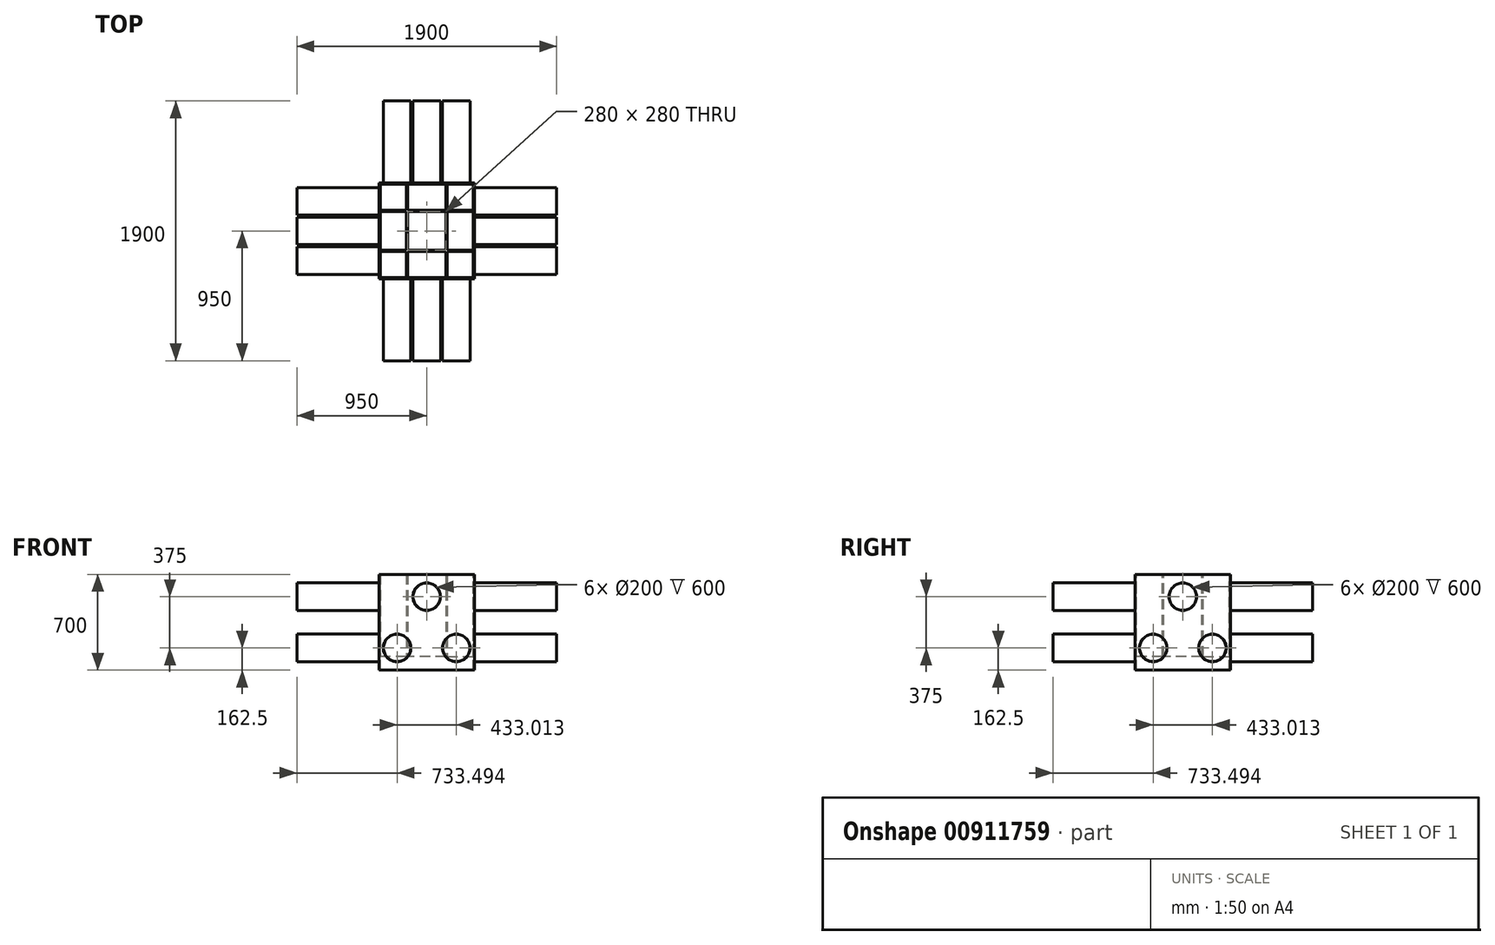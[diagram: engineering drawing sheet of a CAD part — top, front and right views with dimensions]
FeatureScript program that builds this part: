
annotation { "Feature Type Name" : "Feature", "Feature Type Description" : "" }
export const myFeature = defineFeature(function(context is Context, id is Id, definition is map)
    precondition{}
    {
        {
            var Q0;
            Q0=qCreatedBy(makeId("Top.planeOp"),FACE);
            var sketch = newSketch(context, id + "F0", { "sketchPlane" : qUnion([Q0])});
            skLineSegment(sketch, "E0.bottom", {"start": v(350, 350) * mm, "end": v(-350, 350) * mm});
            skLineSegment(sketch, "E0.top", {"start": v(350, -350) * mm, "end": v(-350, -350) * mm});
            skLineSegment(sketch, "E0.left", {"start": v(350, 350) * mm, "end": v(350, -350) * mm});
            skLineSegment(sketch, "E0.right", {"start": v(-350, 350) * mm, "end": v(-350, -350) * mm});
            skPoint(sketch, "E0.middle", {"position": v(0, 0) * mm});
            skLineSegment(sketch, "E1.bottom", {"start": v(340, 340) * mm, "end": v(-340, 340) * mm});
            skLineSegment(sketch, "E1.top", {"start": v(340, -340) * mm, "end": v(-340, -340) * mm});
            skLineSegment(sketch, "E1.left", {"start": v(340, 340) * mm, "end": v(340, -340) * mm});
            skLineSegment(sketch, "E1.right", {"start": v(-340, 340) * mm, "end": v(-340, -340) * mm});
            skSolve(sketch);
        }
        {
            var Q0;
            Q0=makeQuery(id+"F0.imprint","IMPRINT",FACE,{"disambiguationData":[TD([[makeQuery(id+"F0.imprint","IMPRINT",EDGE,{"derivedFrom":sQuery(id+"F0.wireOp",EDGE,"E0.bottom")}),1.0]])]});
            extrude(context, id + "F1", {"entities" : qUnion([Q0]), "oppositeDirection" : true, "depth" : 700 * mm, "offsetDistance" : 25 * mm});
        }
        {
            var Q0;
            Q0=qCreatedBy(makeId("Top.planeOp"),FACE);
            var sketch = newSketch(context, id + "F2", { "sketchPlane" : qUnion([Q0])});
            skLineSegment(sketch, "E2.bottom", {"start": v(-150, 150) * mm, "end": v(150, 150) * mm});
            skLineSegment(sketch, "E2.top", {"start": v(-150, -150) * mm, "end": v(150, -150) * mm});
            skLineSegment(sketch, "E2.left", {"start": v(-150, 150) * mm, "end": v(-150, -150) * mm});
            skLineSegment(sketch, "E2.right", {"start": v(150, 150) * mm, "end": v(150, -150) * mm});
            skPoint(sketch, "E2.middle", {"position": v(0, 0) * mm});
            skLineSegment(sketch, "E3", {"start": v(-150, 150) * mm, "end": v(-150, 300) * mm});
            skLineSegment(sketch, "E4", {"start": v(-150, -150) * mm, "end": v(-150, -300) * mm});
            skLineSegment(sketch, "E5", {"start": v(-150, -150) * mm, "end": v(-300, -150) * mm});
            skLineSegment(sketch, "E6", {"start": v(150, -150) * mm, "end": v(300, -150) * mm});
            skLineSegment(sketch, "E7", {"start": v(150, 150) * mm, "end": v(150, 300) * mm});
            skLineSegment(sketch, "E8", {"start": v(150, 150) * mm, "end": v(300, 150) * mm});
            skLineSegment(sketch, "E9", {"start": v(150, -150) * mm, "end": v(150, -300) * mm});
            skLineSegment(sketch, "E10", {"start": v(-150, 150) * mm, "end": v(-300, 150) * mm});
            skLineSegment(sketch, "E11.bottom", {"start": v(140, 140) * mm, "end": v(-140, 140) * mm});
            skLineSegment(sketch, "E11.top", {"start": v(140, -140) * mm, "end": v(-140, -140) * mm});
            skLineSegment(sketch, "E11.left", {"start": v(140, 140) * mm, "end": v(140, -140) * mm});
            skLineSegment(sketch, "E11.right", {"start": v(-140, 140) * mm, "end": v(-140, -140) * mm});
            skLineSegment(sketch, "E12", {"start": v(-140, 140) * mm, "end": v(-140, 300) * mm});
            skLineSegment(sketch, "E13", {"start": v(140, 140) * mm, "end": v(140, 300) * mm});
            skLineSegment(sketch, "E14", {"start": v(140, 140) * mm, "end": v(300, 140) * mm});
            skLineSegment(sketch, "E15", {"start": v(140, -140) * mm, "end": v(300, -140) * mm});
            skLineSegment(sketch, "E16", {"start": v(140, -140) * mm, "end": v(140, -300) * mm});
            skLineSegment(sketch, "E17", {"start": v(-140, -140) * mm, "end": v(-140, -300) * mm});
            skLineSegment(sketch, "E18", {"start": v(-140, 140) * mm, "end": v(-300, 140) * mm});
            skLineSegment(sketch, "E19", {"start": v(-140, -140) * mm, "end": v(-300, -140) * mm});
            skLineSegment(sketch, "E20", {"start": v(-300, 150) * mm, "end": v(-300, 140) * mm});
            skLineSegment(sketch, "E21", {"start": v(-300, -140) * mm, "end": v(-300, -150) * mm});
            skLineSegment(sketch, "E22", {"start": v(-150, -300) * mm, "end": v(-140, -300) * mm});
            skLineSegment(sketch, "E23", {"start": v(140, -300) * mm, "end": v(150, -300) * mm});
            skLineSegment(sketch, "E24", {"start": v(300, -150) * mm, "end": v(300, -140) * mm});
            skLineSegment(sketch, "E25", {"start": v(300, 140) * mm, "end": v(300, 150) * mm});
            skLineSegment(sketch, "E26", {"start": v(140, 300) * mm, "end": v(150, 300) * mm});
            skLineSegment(sketch, "E27", {"start": v(-150, 300) * mm, "end": v(-140, 300) * mm});
            skSolve(sketch);
        }
        {
            var Q0;
            {var subQ0=sQuery(id+"F2.wireOp",EDGE,"E3");Q0=makeQuery(id+"F2.imprint","IMPRINT",FACE,{"disambiguationData":[TD([[makeQuery(id+"F2.imprint","IMPRINT",EDGE,{"derivedFrom":subQ0}),-1.0]])]});}
            var Q1;
            {var subQ0=sQuery(id+"F2.wireOp",EDGE,"E10");Q1=makeQuery(id+"F2.imprint","IMPRINT",FACE,{"disambiguationData":[TD([[makeQuery(id+"F2.imprint","IMPRINT",EDGE,{"derivedFrom":subQ0}),1.0]])]});}
            var Q2;
            {var subQ1=sQuery(id+"F2.wireOp",EDGE,"E2.bottom");var subQ3=sQuery(id+"F2.wireOp",EDGE,"E12");var subQ4=makeQuery(id+"F2.imprint","INTERSECT",VERTEX,{"derivedFrom":[subQ1,subQ3]});Q2=makeQuery(id+"F2.imprint","IMPRINT",FACE,{"disambiguationData":[TD([[makeQuery(id+"F2.imprint","IMPRINT",EDGE,{"disambiguationData":[TD([[subQ4,1.0]])],"derivedFrom":subQ1}),-1.0]])]});}
            var Q3;
            {var subQ5=sQuery(id+"F2.wireOp",EDGE,"E11.bottom");Q3=makeQuery(id+"F2.imprint","IMPRINT",FACE,{"disambiguationData":[TD([[makeQuery(id+"F2.imprint","IMPRINT",EDGE,{"derivedFrom":subQ5}),-1.0]])]});}
            var Q4;
            {var subQ5=sQuery(id+"F2.wireOp",EDGE,"E11.right");Q4=makeQuery(id+"F2.imprint","IMPRINT",FACE,{"disambiguationData":[TD([[makeQuery(id+"F2.imprint","IMPRINT",EDGE,{"derivedFrom":subQ5}),-1.0]])]});}
            var Q5;
            {var subQ0=sQuery(id+"F2.wireOp",EDGE,"E7");Q5=makeQuery(id+"F2.imprint","IMPRINT",FACE,{"disambiguationData":[TD([[makeQuery(id+"F2.imprint","IMPRINT",EDGE,{"derivedFrom":subQ0}),1.0]])]});}
            var Q6;
            {var subQ0=sQuery(id+"F2.wireOp",EDGE,"E8");Q6=makeQuery(id+"F2.imprint","IMPRINT",FACE,{"disambiguationData":[TD([[makeQuery(id+"F2.imprint","IMPRINT",EDGE,{"derivedFrom":subQ0}),-1.0]])]});}
            var Q7;
            {var subQ1=sQuery(id+"F2.wireOp",EDGE,"E2.bottom");var subQ3=sQuery(id+"F2.wireOp",EDGE,"E13");var subQ4=makeQuery(id+"F2.imprint","INTERSECT",VERTEX,{"derivedFrom":[subQ1,subQ3]});Q7=makeQuery(id+"F2.imprint","IMPRINT",FACE,{"disambiguationData":[TD([[makeQuery(id+"F2.imprint","IMPRINT",EDGE,{"disambiguationData":[TD([[subQ4,-1.0]])],"derivedFrom":subQ1}),-1.0]])]});}
            var Q8;
            {var subQ0=sQuery(id+"F2.wireOp",EDGE,"E9");Q8=makeQuery(id+"F2.imprint","IMPRINT",FACE,{"disambiguationData":[TD([[makeQuery(id+"F2.imprint","IMPRINT",EDGE,{"derivedFrom":subQ0}),-1.0]])]});}
            var Q9;
            {var subQ0=sQuery(id+"F2.wireOp",EDGE,"E6");Q9=makeQuery(id+"F2.imprint","IMPRINT",FACE,{"disambiguationData":[TD([[makeQuery(id+"F2.imprint","IMPRINT",EDGE,{"derivedFrom":subQ0}),1.0]])]});}
            var Q10;
            {var subQ1=sQuery(id+"F2.wireOp",EDGE,"E2.top");var subQ3=sQuery(id+"F2.wireOp",EDGE,"E16");var subQ4=makeQuery(id+"F2.imprint","INTERSECT",VERTEX,{"derivedFrom":[subQ1,subQ3]});Q10=makeQuery(id+"F2.imprint","IMPRINT",FACE,{"disambiguationData":[TD([[makeQuery(id+"F2.imprint","IMPRINT",EDGE,{"disambiguationData":[TD([[subQ4,-1.0]])],"derivedFrom":subQ1}),1.0]])]});}
            var Q11;
            {var subQ5=sQuery(id+"F2.wireOp",EDGE,"E11.left");Q11=makeQuery(id+"F2.imprint","IMPRINT",FACE,{"disambiguationData":[TD([[makeQuery(id+"F2.imprint","IMPRINT",EDGE,{"derivedFrom":subQ5}),1.0]])]});}
            var Q12;
            {var subQ5=sQuery(id+"F2.wireOp",EDGE,"E11.top");Q12=makeQuery(id+"F2.imprint","IMPRINT",FACE,{"disambiguationData":[TD([[makeQuery(id+"F2.imprint","IMPRINT",EDGE,{"derivedFrom":subQ5}),1.0]])]});}
            var Q13;
            {var subQ0=sQuery(id+"F2.wireOp",EDGE,"E5");Q13=makeQuery(id+"F2.imprint","IMPRINT",FACE,{"disambiguationData":[TD([[makeQuery(id+"F2.imprint","IMPRINT",EDGE,{"derivedFrom":subQ0}),-1.0]])]});}
            var Q14;
            {var subQ0=sQuery(id+"F2.wireOp",EDGE,"E4");Q14=makeQuery(id+"F2.imprint","IMPRINT",FACE,{"disambiguationData":[TD([[makeQuery(id+"F2.imprint","IMPRINT",EDGE,{"derivedFrom":subQ0}),1.0]])]});}
            var Q15;
            {var subQ1=sQuery(id+"F2.wireOp",EDGE,"E2.top");var subQ3=sQuery(id+"F2.wireOp",EDGE,"E17");var subQ4=makeQuery(id+"F2.imprint","INTERSECT",VERTEX,{"derivedFrom":[subQ1,subQ3]});Q15=makeQuery(id+"F2.imprint","IMPRINT",FACE,{"disambiguationData":[TD([[makeQuery(id+"F2.imprint","IMPRINT",EDGE,{"disambiguationData":[TD([[subQ4,1.0]])],"derivedFrom":subQ1}),1.0]])]});}
            extrude(context, id + "F3", {"entities" : qUnion([Q0, Q1, Q2, Q3, Q4, Q5, Q6, Q7, Q8, Q9, Q10, Q11, Q12, Q13, Q14, Q15]), "operationType" : NewBodyOperationType.ADD, "oppositeDirection" : true, "depth" : 600 * mm, "offsetDistance" : 25 * mm});
        }
        {
            var Q0;
            Q0=makeQuery(id+"F1.opExtrude","SWEPT_FACE",FACE,{"disambiguationData":[OSD([sQuery(id+"F0.wireOp",EDGE,"E0.left")])]});
            var sketch = newSketch(context, id + "F4", { "sketchPlane" : qUnion([Q0])});
            skPoint(sketch, "E28", {"position": v(0, -350) * mm});
            skPoint(sketch, "E28.positionSnap0", {"position": v(-350, -350) * mm});
            skPoint(sketch, "E28.positionSnap1", {"position": v(0, 0) * mm});
            skCircle(sketch, "E29.cCircle", {"center": v(0, -412.5) * mm, "radius": 250 * mm, "construction": true});
            skLineSegment(sketch, "E29.0", {"start": v(0, -162.5) * mm, "end": v(216.5, -537.5) * mm});
            skLineSegment(sketch, "E29.1", {"start": v(216.5, -537.5) * mm, "end": v(-216.5, -537.5) * mm});
            skLineSegment(sketch, "E29.2", {"start": v(-216.5, -537.5) * mm, "end": v(0, -162.5) * mm});
            skCircle(sketch, "E30", {"center": v(0, -162.5) * mm, "radius": 100 * mm});
            skCircle(sketch, "E31", {"center": v(216.5, -537.5) * mm, "radius": 100 * mm});
            skCircle(sketch, "E32", {"center": v(-216.5, -537.5) * mm, "radius": 100 * mm});
            skCircle(sketch, "E33", {"center": v(0, -162.5) * mm, "radius": 101 * mm});
            skCircle(sketch, "E34", {"center": v(-216.5, -537.5) * mm, "radius": 101 * mm});
            skCircle(sketch, "E35", {"center": v(216.5, -537.5) * mm, "radius": 101 * mm});
            skSolve(sketch);
        }
        {
            var Q0;
            Q0=makeQuery(id+"F1.opExtrude","SWEPT_FACE",FACE,{"disambiguationData":[OSD([sQuery(id+"F0.wireOp",EDGE,"E0.top")])]});
            var sketch = newSketch(context, id + "F5", { "sketchPlane" : qUnion([Q0])});
            skPoint(sketch, "E36", {"position": v(0, -412.5) * mm});
            skPoint(sketch, "E36.positionSnap0", {"position": v(-350, -412.5) * mm});
            skPoint(sketch, "E36.positionSnap1", {"position": v(0, 157.53) * mm});
            skCircle(sketch, "E37.cCircle", {"center": v(0, -412.5) * mm, "radius": 250 * mm, "construction": true});
            skLineSegment(sketch, "E37.0", {"start": v(0, -162.5) * mm, "end": v(216.5, -537.5) * mm});
            skLineSegment(sketch, "E37.1", {"start": v(216.5, -537.5) * mm, "end": v(-216.5, -537.5) * mm});
            skLineSegment(sketch, "E37.2", {"start": v(-216.5, -537.5) * mm, "end": v(0, -162.5) * mm});
            skCircle(sketch, "E38", {"center": v(0, -162.5) * mm, "radius": 100 * mm});
            skCircle(sketch, "E39", {"center": v(216.5, -537.5) * mm, "radius": 100 * mm});
            skCircle(sketch, "E40", {"center": v(-216.5, -537.5) * mm, "radius": 100 * mm});
            skCircle(sketch, "E41", {"center": v(0, -162.5) * mm, "radius": 101 * mm});
            skCircle(sketch, "E42", {"center": v(-216.5, -537.5) * mm, "radius": 101 * mm});
            skCircle(sketch, "E43", {"center": v(216.5, -537.5) * mm, "radius": 101 * mm});
            skSolve(sketch);
        }
        {
            var Q0;
            Q0=makeQuery(id+"F1.opExtrude","SWEPT_FACE",FACE,{"disambiguationData":[OSD([sQuery(id+"F0.wireOp",EDGE,"E0.right")])]});
            var sketch = newSketch(context, id + "F6", { "sketchPlane" : qUnion([Q0])});
            skPoint(sketch, "E44", {"position": v(0, -350) * mm});
            skPoint(sketch, "E44.positionSnap0", {"position": v(-350, -350) * mm});
            skPoint(sketch, "E44.positionSnap1", {"position": v(0, 0) * mm});
            skCircle(sketch, "E45.cCircle", {"center": v(0, -412.5) * mm, "radius": 250 * mm, "construction": true});
            skLineSegment(sketch, "E45.0", {"start": v(0, -162.5) * mm, "end": v(216.5, -537.5) * mm});
            skLineSegment(sketch, "E45.1", {"start": v(216.5, -537.5) * mm, "end": v(-216.5, -537.5) * mm});
            skLineSegment(sketch, "E45.2", {"start": v(-216.5, -537.5) * mm, "end": v(0, -162.5) * mm});
            skCircle(sketch, "E46", {"center": v(0, -162.5) * mm, "radius": 100 * mm});
            skCircle(sketch, "E47", {"center": v(216.5, -537.5) * mm, "radius": 100 * mm});
            skCircle(sketch, "E48", {"center": v(-216.5, -537.5) * mm, "radius": 100 * mm});
            skCircle(sketch, "E49", {"center": v(0, -162.5) * mm, "radius": 101 * mm});
            skCircle(sketch, "E50", {"center": v(-216.5, -537.5) * mm, "radius": 101 * mm});
            skCircle(sketch, "E51", {"center": v(216.5, -537.5) * mm, "radius": 101 * mm});
            skSolve(sketch);
        }
        {
            var Q0;
            Q0=makeQuery(id+"F1.opExtrude","SWEPT_FACE",FACE,{"disambiguationData":[OSD([sQuery(id+"F0.wireOp",EDGE,"E0.bottom")])]});
            var sketch = newSketch(context, id + "F7", { "sketchPlane" : qUnion([Q0])});
            skPoint(sketch, "E52", {"position": v(0, -350) * mm});
            skPoint(sketch, "E52.positionSnap0", {"position": v(-350, -350) * mm});
            skPoint(sketch, "E52.positionSnap1", {"position": v(0, 0) * mm});
            skCircle(sketch, "E53.cCircle", {"center": v(0, -412.5) * mm, "radius": 250 * mm, "construction": true});
            skLineSegment(sketch, "E53.0", {"start": v(0, -162.5) * mm, "end": v(216.5, -537.5) * mm});
            skLineSegment(sketch, "E53.1", {"start": v(216.5, -537.5) * mm, "end": v(-216.5, -537.5) * mm});
            skLineSegment(sketch, "E53.2", {"start": v(-216.5, -537.5) * mm, "end": v(0, -162.5) * mm});
            skCircle(sketch, "E54", {"center": v(0, -162.5) * mm, "radius": 100 * mm});
            skCircle(sketch, "E55", {"center": v(216.5, -537.5) * mm, "radius": 100 * mm});
            skCircle(sketch, "E56", {"center": v(-216.5, -537.5) * mm, "radius": 100 * mm});
            skCircle(sketch, "E57", {"center": v(0, -162.5) * mm, "radius": 101 * mm});
            skCircle(sketch, "E58", {"center": v(216.5, -537.5) * mm, "radius": 101 * mm});
            skCircle(sketch, "E59", {"center": v(-216.5, -537.5) * mm, "radius": 101 * mm});
            skSolve(sketch);
        }
        {
            var Q0;
            Q0=makeQuery(id+"F3.opExtrude","SWEPT_FACE",FACE,{"disambiguationData":[OSD([sQuery(id+"F2.wireOp",EDGE,"E20")])]});
            extrude(context, id + "F8", {"entities" : qUnion([Q0]), "depth" : 50 * mm, "offsetDistance" : 25 * mm});
        }
        {
            var Q0;
            Q0=makeQuery(id+"F3.opExtrude","SWEPT_FACE",FACE,{"disambiguationData":[OSD([sQuery(id+"F2.wireOp",EDGE,"E22")])]});
            extrude(context, id + "F9", {"entities" : qUnion([Q0]), "depth" : 50 * mm, "offsetDistance" : 25 * mm});
        }
        {
            var Q0;
            Q0=makeQuery(id+"F3.opExtrude","SWEPT_FACE",FACE,{"disambiguationData":[OSD([sQuery(id+"F2.wireOp",EDGE,"E21")])]});
            extrude(context, id + "F10", {"entities" : qUnion([Q0]), "operationType" : NewBodyOperationType.ADD, "depth" : 50 * mm, "offsetDistance" : 25 * mm});
        }
        {
            var Q0;
            Q0=makeQuery(id+"F3.opExtrude","SWEPT_FACE",FACE,{"disambiguationData":[OSD([sQuery(id+"F2.wireOp",EDGE,"E23")])]});
            extrude(context, id + "F11", {"entities" : qUnion([Q0]), "depth" : 50 * mm, "offsetDistance" : 25 * mm});
        }
        {
            var Q0;
            Q0=makeQuery(id+"F3.opExtrude","SWEPT_FACE",FACE,{"disambiguationData":[OSD([sQuery(id+"F2.wireOp",EDGE,"E24")])]});
            extrude(context, id + "F12", {"entities" : qUnion([Q0]), "depth" : 50 * mm, "offsetDistance" : 25 * mm});
        }
        {
            var Q0;
            Q0=makeQuery(id+"F3.opExtrude","SWEPT_FACE",FACE,{"disambiguationData":[OSD([sQuery(id+"F2.wireOp",EDGE,"E25")])]});
            extrude(context, id + "F13", {"entities" : qUnion([Q0]), "depth" : 50 * mm, "offsetDistance" : 25 * mm});
        }
        {
            var Q0;
            Q0=makeQuery(id+"F3.opExtrude","SWEPT_FACE",FACE,{"disambiguationData":[OSD([sQuery(id+"F2.wireOp",EDGE,"E26")])]});
            extrude(context, id + "F14", {"entities" : qUnion([Q0]), "depth" : 50 * mm, "offsetDistance" : 25 * mm});
        }
        {
            var Q0;
            Q0=makeQuery(id+"F3.opExtrude","SWEPT_FACE",FACE,{"disambiguationData":[OSD([sQuery(id+"F2.wireOp",EDGE,"E27")])]});
            extrude(context, id + "F15", {"entities" : qUnion([Q0]), "depth" : 50 * mm, "offsetDistance" : 25 * mm});
        }
        {
            var Q0;
            {var subQ0=sQuery(id+"F4.wireOp",EDGE,"E30");var subQ1=sQuery(id+"F4.wireOp",EDGE,"E29.0");var subQ2=makeQuery(id+"F4.imprint","INTERSECT",VERTEX,{"derivedFrom":[subQ1,subQ0]});Q0=makeQuery(id+"F4.imprint","IMPRINT",FACE,{"disambiguationData":[TD([[makeQuery(id+"F4.imprint","IMPRINT",EDGE,{"disambiguationData":[TD([[subQ2,-1.0]])],"derivedFrom":subQ1}),1.0]])]});}
            var Q1;
            {var subQ0=sQuery(id+"F4.wireOp",EDGE,"E35");var subQ1=sQuery(id+"F4.wireOp",EDGE,"E29.0");var subQ2=makeQuery(id+"F4.imprint","INTERSECT",VERTEX,{"derivedFrom":[subQ1,subQ0]});Q1=makeQuery(id+"F4.imprint","IMPRINT",FACE,{"disambiguationData":[TD([[makeQuery(id+"F4.imprint","IMPRINT",EDGE,{"disambiguationData":[TD([[subQ2,-1.0]])],"derivedFrom":subQ1}),1.0]])]});}
            var Q2;
            {var subQ0=sQuery(id+"F4.wireOp",EDGE,"E35");var subQ1=sQuery(id+"F4.wireOp",EDGE,"E29.0");var subQ2=makeQuery(id+"F4.imprint","INTERSECT",VERTEX,{"derivedFrom":[subQ1,subQ0]});Q2=makeQuery(id+"F4.imprint","IMPRINT",FACE,{"disambiguationData":[TD([[makeQuery(id+"F4.imprint","IMPRINT",EDGE,{"disambiguationData":[TD([[subQ2,-1.0]])],"derivedFrom":subQ1}),-1.0]])]});}
            var Q3;
            {var subQ0=sQuery(id+"F4.wireOp",EDGE,"E30");var subQ1=sQuery(id+"F4.wireOp",EDGE,"E29.0");var subQ2=makeQuery(id+"F4.imprint","INTERSECT",VERTEX,{"derivedFrom":[subQ1,subQ0]});Q3=makeQuery(id+"F4.imprint","IMPRINT",FACE,{"disambiguationData":[TD([[makeQuery(id+"F4.imprint","IMPRINT",EDGE,{"disambiguationData":[TD([[subQ2,-1.0]])],"derivedFrom":subQ1}),-1.0]])]});}
            var Q4;
            {var subQ0=sQuery(id+"F4.wireOp",EDGE,"E34");var subQ1=sQuery(id+"F4.wireOp",EDGE,"E29.1");var subQ2=makeQuery(id+"F4.imprint","INTERSECT",VERTEX,{"derivedFrom":[subQ1,subQ0]});Q4=makeQuery(id+"F4.imprint","IMPRINT",FACE,{"disambiguationData":[TD([[makeQuery(id+"F4.imprint","IMPRINT",EDGE,{"disambiguationData":[TD([[subQ2,-1.0]])],"derivedFrom":subQ1}),1.0]])]});}
            var Q5;
            {var subQ0=sQuery(id+"F4.wireOp",EDGE,"E34");var subQ1=sQuery(id+"F4.wireOp",EDGE,"E29.1");var subQ2=makeQuery(id+"F4.imprint","INTERSECT",VERTEX,{"derivedFrom":[subQ1,subQ0]});Q5=makeQuery(id+"F4.imprint","IMPRINT",FACE,{"disambiguationData":[TD([[makeQuery(id+"F4.imprint","IMPRINT",EDGE,{"disambiguationData":[TD([[subQ2,-1.0]])],"derivedFrom":subQ1}),-1.0]])]});}
            extrude(context, id + "F16", {"entities" : qUnion([Q0, Q1, Q2, Q3, Q4, Q5]), "operationType" : NewBodyOperationType.ADD, "depth" : 600 * mm, "offsetDistance" : 25 * mm});
        }
        {
            var Q0;
            {var subQ0=sQuery(id+"F5.wireOp",EDGE,"E38");var subQ1=sQuery(id+"F5.wireOp",EDGE,"E37.0");var subQ2=makeQuery(id+"F5.imprint","INTERSECT",VERTEX,{"derivedFrom":[subQ1,subQ0]});Q0=makeQuery(id+"F5.imprint","IMPRINT",FACE,{"disambiguationData":[TD([[makeQuery(id+"F5.imprint","IMPRINT",EDGE,{"disambiguationData":[TD([[subQ2,-1.0]])],"derivedFrom":subQ1}),-1.0]])]});}
            var Q1;
            {var subQ0=sQuery(id+"F5.wireOp",EDGE,"E38");var subQ1=sQuery(id+"F5.wireOp",EDGE,"E37.0");var subQ2=makeQuery(id+"F5.imprint","INTERSECT",VERTEX,{"derivedFrom":[subQ1,subQ0]});Q1=makeQuery(id+"F5.imprint","IMPRINT",FACE,{"disambiguationData":[TD([[makeQuery(id+"F5.imprint","IMPRINT",EDGE,{"disambiguationData":[TD([[subQ2,-1.0]])],"derivedFrom":subQ1}),1.0]])]});}
            var Q2;
            {var subQ0=sQuery(id+"F5.wireOp",EDGE,"E42");var subQ1=sQuery(id+"F5.wireOp",EDGE,"E37.1");var subQ2=makeQuery(id+"F5.imprint","INTERSECT",VERTEX,{"derivedFrom":[subQ1,subQ0]});Q2=makeQuery(id+"F5.imprint","IMPRINT",FACE,{"disambiguationData":[TD([[makeQuery(id+"F5.imprint","IMPRINT",EDGE,{"disambiguationData":[TD([[subQ2,-1.0]])],"derivedFrom":subQ1}),1.0]])]});}
            var Q3;
            {var subQ0=sQuery(id+"F5.wireOp",EDGE,"E42");var subQ1=sQuery(id+"F5.wireOp",EDGE,"E37.1");var subQ2=makeQuery(id+"F5.imprint","INTERSECT",VERTEX,{"derivedFrom":[subQ1,subQ0]});Q3=makeQuery(id+"F5.imprint","IMPRINT",FACE,{"disambiguationData":[TD([[makeQuery(id+"F5.imprint","IMPRINT",EDGE,{"disambiguationData":[TD([[subQ2,-1.0]])],"derivedFrom":subQ1}),-1.0]])]});}
            var Q4;
            {var subQ0=sQuery(id+"F5.wireOp",EDGE,"E43");var subQ1=sQuery(id+"F5.wireOp",EDGE,"E37.0");var subQ2=makeQuery(id+"F5.imprint","INTERSECT",VERTEX,{"derivedFrom":[subQ1,subQ0]});Q4=makeQuery(id+"F5.imprint","IMPRINT",FACE,{"disambiguationData":[TD([[makeQuery(id+"F5.imprint","IMPRINT",EDGE,{"disambiguationData":[TD([[subQ2,-1.0]])],"derivedFrom":subQ1}),1.0]])]});}
            var Q5;
            {var subQ0=sQuery(id+"F5.wireOp",EDGE,"E43");var subQ1=sQuery(id+"F5.wireOp",EDGE,"E37.0");var subQ2=makeQuery(id+"F5.imprint","INTERSECT",VERTEX,{"derivedFrom":[subQ1,subQ0]});Q5=makeQuery(id+"F5.imprint","IMPRINT",FACE,{"disambiguationData":[TD([[makeQuery(id+"F5.imprint","IMPRINT",EDGE,{"disambiguationData":[TD([[subQ2,-1.0]])],"derivedFrom":subQ1}),-1.0]])]});}
            extrude(context, id + "F17", {"entities" : qUnion([Q0, Q1, Q2, Q3, Q4, Q5]), "operationType" : NewBodyOperationType.ADD, "depth" : 600 * mm, "offsetDistance" : 25 * mm});
        }
        {
            var Q0;
            {var subQ0=sQuery(id+"F6.wireOp",EDGE,"E46");var subQ1=sQuery(id+"F6.wireOp",EDGE,"E45.0");var subQ2=makeQuery(id+"F6.imprint","INTERSECT",VERTEX,{"derivedFrom":[subQ1,subQ0]});Q0=makeQuery(id+"F6.imprint","IMPRINT",FACE,{"disambiguationData":[TD([[makeQuery(id+"F6.imprint","IMPRINT",EDGE,{"disambiguationData":[TD([[subQ2,-1.0]])],"derivedFrom":subQ1}),1.0]])]});}
            var Q1;
            {var subQ0=sQuery(id+"F6.wireOp",EDGE,"E46");var subQ1=sQuery(id+"F6.wireOp",EDGE,"E45.0");var subQ2=makeQuery(id+"F6.imprint","INTERSECT",VERTEX,{"derivedFrom":[subQ1,subQ0]});Q1=makeQuery(id+"F6.imprint","IMPRINT",FACE,{"disambiguationData":[TD([[makeQuery(id+"F6.imprint","IMPRINT",EDGE,{"disambiguationData":[TD([[subQ2,-1.0]])],"derivedFrom":subQ1}),-1.0]])]});}
            var Q2;
            {var subQ0=sQuery(id+"F6.wireOp",EDGE,"E51");var subQ1=sQuery(id+"F6.wireOp",EDGE,"E45.0");var subQ2=makeQuery(id+"F6.imprint","INTERSECT",VERTEX,{"derivedFrom":[subQ1,subQ0]});Q2=makeQuery(id+"F6.imprint","IMPRINT",FACE,{"disambiguationData":[TD([[makeQuery(id+"F6.imprint","IMPRINT",EDGE,{"disambiguationData":[TD([[subQ2,-1.0]])],"derivedFrom":subQ1}),1.0]])]});}
            var Q3;
            {var subQ0=sQuery(id+"F6.wireOp",EDGE,"E51");var subQ1=sQuery(id+"F6.wireOp",EDGE,"E45.0");var subQ2=makeQuery(id+"F6.imprint","INTERSECT",VERTEX,{"derivedFrom":[subQ1,subQ0]});Q3=makeQuery(id+"F6.imprint","IMPRINT",FACE,{"disambiguationData":[TD([[makeQuery(id+"F6.imprint","IMPRINT",EDGE,{"disambiguationData":[TD([[subQ2,-1.0]])],"derivedFrom":subQ1}),-1.0]])]});}
            var Q4;
            {var subQ0=sQuery(id+"F6.wireOp",EDGE,"E50");var subQ1=sQuery(id+"F6.wireOp",EDGE,"E45.1");var subQ2=makeQuery(id+"F6.imprint","INTERSECT",VERTEX,{"derivedFrom":[subQ1,subQ0]});Q4=makeQuery(id+"F6.imprint","IMPRINT",FACE,{"disambiguationData":[TD([[makeQuery(id+"F6.imprint","IMPRINT",EDGE,{"disambiguationData":[TD([[subQ2,-1.0]])],"derivedFrom":subQ1}),1.0]])]});}
            var Q5;
            {var subQ0=sQuery(id+"F6.wireOp",EDGE,"E50");var subQ1=sQuery(id+"F6.wireOp",EDGE,"E45.1");var subQ2=makeQuery(id+"F6.imprint","INTERSECT",VERTEX,{"derivedFrom":[subQ1,subQ0]});Q5=makeQuery(id+"F6.imprint","IMPRINT",FACE,{"disambiguationData":[TD([[makeQuery(id+"F6.imprint","IMPRINT",EDGE,{"disambiguationData":[TD([[subQ2,-1.0]])],"derivedFrom":subQ1}),-1.0]])]});}
            extrude(context, id + "F18", {"entities" : qUnion([Q0, Q1, Q2, Q3, Q4, Q5]), "operationType" : NewBodyOperationType.ADD, "depth" : 600 * mm, "offsetDistance" : 25 * mm});
        }
        {
            var Q0;
            {var subQ0=sQuery(id+"F7.wireOp",EDGE,"E54");var subQ1=sQuery(id+"F7.wireOp",EDGE,"E53.0");var subQ2=makeQuery(id+"F7.imprint","INTERSECT",VERTEX,{"derivedFrom":[subQ1,subQ0]});Q0=makeQuery(id+"F7.imprint","IMPRINT",FACE,{"disambiguationData":[TD([[makeQuery(id+"F7.imprint","IMPRINT",EDGE,{"disambiguationData":[TD([[subQ2,-1.0]])],"derivedFrom":subQ1}),-1.0]])]});}
            var Q1;
            {var subQ0=sQuery(id+"F7.wireOp",EDGE,"E54");var subQ1=sQuery(id+"F7.wireOp",EDGE,"E53.0");var subQ2=makeQuery(id+"F7.imprint","INTERSECT",VERTEX,{"derivedFrom":[subQ1,subQ0]});Q1=makeQuery(id+"F7.imprint","IMPRINT",FACE,{"disambiguationData":[TD([[makeQuery(id+"F7.imprint","IMPRINT",EDGE,{"disambiguationData":[TD([[subQ2,-1.0]])],"derivedFrom":subQ1}),1.0]])]});}
            var Q2;
            {var subQ0=sQuery(id+"F7.wireOp",EDGE,"E59");var subQ1=sQuery(id+"F7.wireOp",EDGE,"E53.1");var subQ2=makeQuery(id+"F7.imprint","INTERSECT",VERTEX,{"derivedFrom":[subQ1,subQ0]});Q2=makeQuery(id+"F7.imprint","IMPRINT",FACE,{"disambiguationData":[TD([[makeQuery(id+"F7.imprint","IMPRINT",EDGE,{"disambiguationData":[TD([[subQ2,-1.0]])],"derivedFrom":subQ1}),1.0]])]});}
            var Q3;
            {var subQ0=sQuery(id+"F7.wireOp",EDGE,"E59");var subQ1=sQuery(id+"F7.wireOp",EDGE,"E53.1");var subQ2=makeQuery(id+"F7.imprint","INTERSECT",VERTEX,{"derivedFrom":[subQ1,subQ0]});Q3=makeQuery(id+"F7.imprint","IMPRINT",FACE,{"disambiguationData":[TD([[makeQuery(id+"F7.imprint","IMPRINT",EDGE,{"disambiguationData":[TD([[subQ2,-1.0]])],"derivedFrom":subQ1}),-1.0]])]});}
            var Q4;
            {var subQ0=sQuery(id+"F7.wireOp",EDGE,"E58");var subQ1=sQuery(id+"F7.wireOp",EDGE,"E53.0");var subQ2=makeQuery(id+"F7.imprint","INTERSECT",VERTEX,{"derivedFrom":[subQ1,subQ0]});Q4=makeQuery(id+"F7.imprint","IMPRINT",FACE,{"disambiguationData":[TD([[makeQuery(id+"F7.imprint","IMPRINT",EDGE,{"disambiguationData":[TD([[subQ2,-1.0]])],"derivedFrom":subQ1}),-1.0]])]});}
            var Q5;
            {var subQ0=sQuery(id+"F7.wireOp",EDGE,"E58");var subQ1=sQuery(id+"F7.wireOp",EDGE,"E53.0");var subQ2=makeQuery(id+"F7.imprint","INTERSECT",VERTEX,{"derivedFrom":[subQ1,subQ0]});Q5=makeQuery(id+"F7.imprint","IMPRINT",FACE,{"disambiguationData":[TD([[makeQuery(id+"F7.imprint","IMPRINT",EDGE,{"disambiguationData":[TD([[subQ2,-1.0]])],"derivedFrom":subQ1}),1.0]])]});}
            extrude(context, id + "F19", {"entities" : qUnion([Q0, Q1, Q2, Q3, Q4, Q5]), "operationType" : NewBodyOperationType.ADD, "depth" : 600 * mm, "offsetDistance" : 25 * mm});
        }
    });
